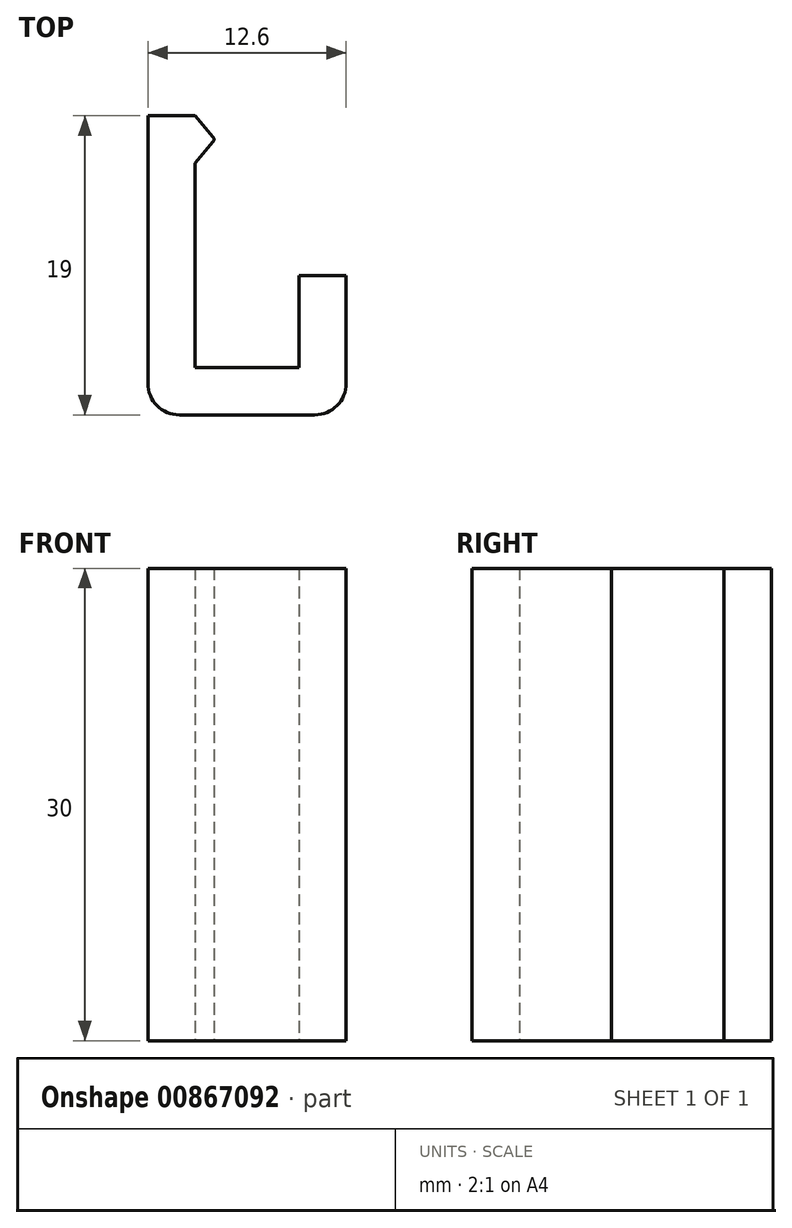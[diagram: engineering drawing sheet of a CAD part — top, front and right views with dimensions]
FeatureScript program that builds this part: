
annotation { "Feature Type Name" : "Feature", "Feature Type Description" : "" }
export const myFeature = defineFeature(function(context is Context, id is Id, definition is map)
    precondition{}
    {
        {
            var Q0;
            Q0=qCreatedBy(makeId("Top.planeOp"),FACE);
            var sketch = newSketch(context, id + "F0", { "sketchPlane" : qUnion([Q0])});
            skLineSegment(sketch, "E0", {"start": v(0.7, 19.75) * mm, "end": v(0.7, 2.75) * mm});
            skLineSegment(sketch, "E1", {"start": v(2.7, 0.75) * mm, "end": v(11.3, 0.75) * mm});
            skLineSegment(sketch, "E2", {"start": v(13.3, 2.75) * mm, "end": v(13.3, 9.6) * mm});
            skLineSegment(sketch, "E3.0", {"start": v(10.3, 3.75) * mm, "end": v(10.3, 9.6) * mm});
            skLineSegment(sketch, "E3.1", {"start": v(3.7, 3.75) * mm, "end": v(10.3, 3.75) * mm});
            skLineSegment(sketch, "E3.2", {"start": v(3.7, 16.75) * mm, "end": v(3.7, 3.75) * mm});
            skLineSegment(sketch, "E4", {"start": v(10.3, 9.6) * mm, "end": v(13.3, 9.6) * mm});
            skLineSegment(sketch, "E5", {"start": v(0.7, 19.75) * mm, "end": v(3.7, 19.75) * mm});
            skLineSegment(sketch, "E6", {"start": v(3.7, 19.75) * mm, "end": v(4.85, 18.38) * mm});
            skLineSegment(sketch, "E7", {"start": v(4.85, 18.12) * mm, "end": v(3.7, 16.75) * mm});
            skPoint(sketch, "E8.visualSharp", {"position": v(4.96, 18.25) * mm});
            skArc(sketch, "E8.filletArc", {"start": v(4.85, 18.12) * mm, "mid": v(4.9, 18.25) * mm, "end": v(4.85, 18.38) * mm});
            skLineSegment(sketch, "E9", {"start": v(4.9, 39.6) * mm, "end": v(4.9, 43.13) * mm, "construction": true});
            skPoint(sketch, "E10.visualSharp", {"position": v(0.7, 0.75) * mm});
            skArc(sketch, "E10.filletArc", {"start": v(0.7, 2.75) * mm, "mid": v(1.29, 1.33) * mm, "end": v(2.7, 0.75) * mm});
            skPoint(sketch, "E11.visualSharp", {"position": v(13.3, 0.75) * mm});
            skArc(sketch, "E11.filletArc", {"start": v(11.3, 0.75) * mm, "mid": v(12.71, 1.33) * mm, "end": v(13.3, 2.75) * mm});
            skSolve(sketch);
        }
        {
            var Q0;
            Q0 = qSketchRegion(id + "F0", true);
            extrude(context, id + "F1", {"entities" : qUnion([Q0]), "depth" : 30 * mm, "offsetDistance" : 25 * mm});
        }
    });
